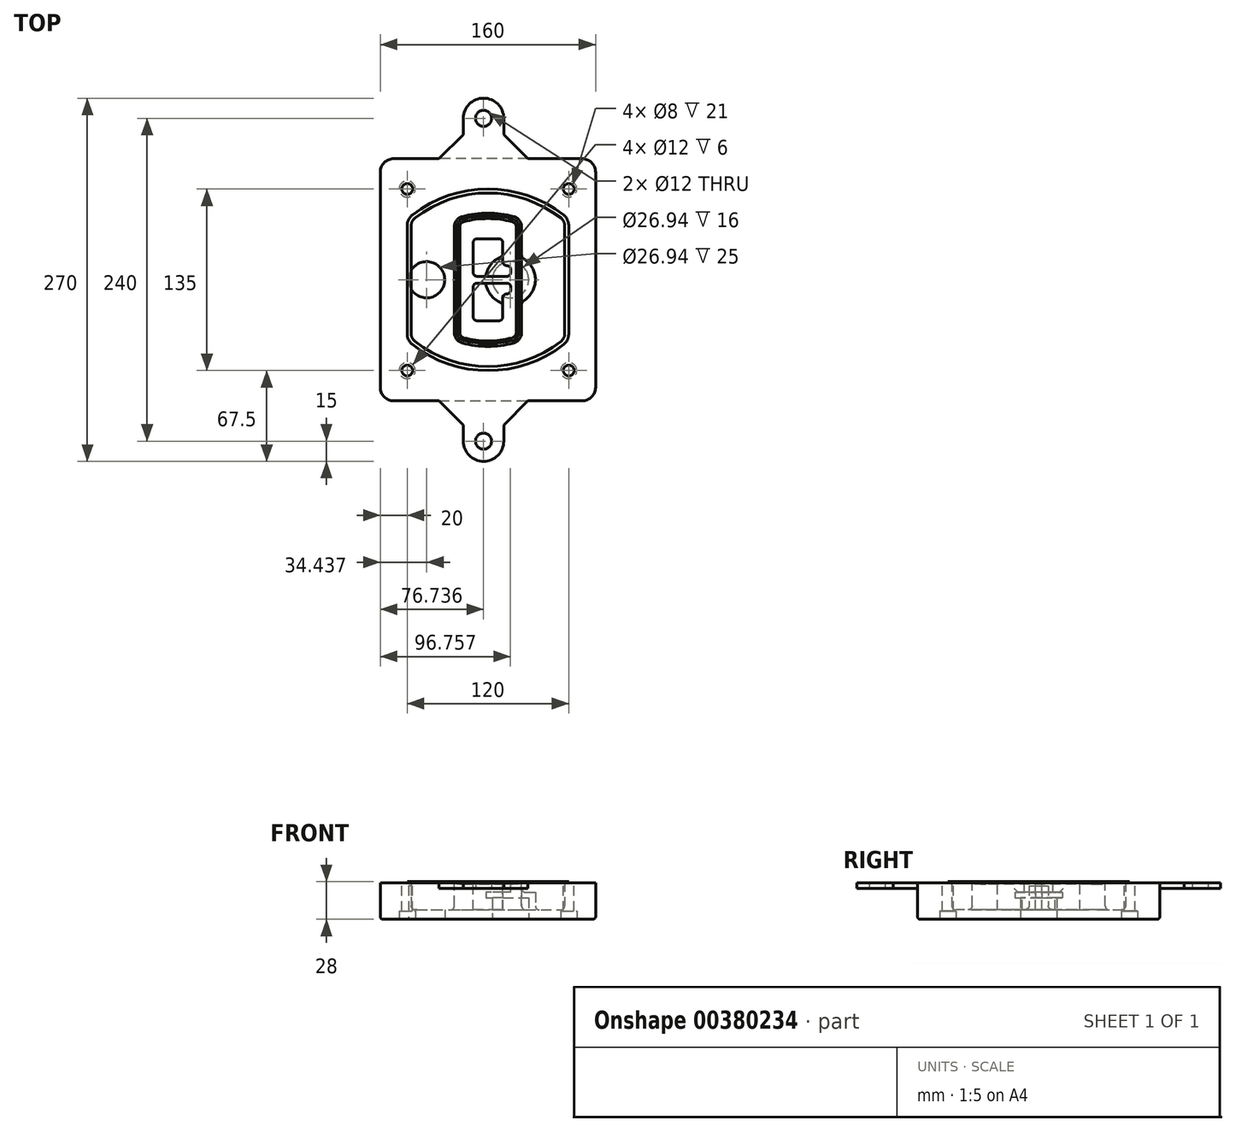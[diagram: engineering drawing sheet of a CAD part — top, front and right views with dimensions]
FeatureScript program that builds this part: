
annotation { "Feature Type Name" : "Feature", "Feature Type Description" : "" }
export const myFeature = defineFeature(function(context is Context, id is Id, definition is map)
    precondition{}
    {
        {
            var Q0;
            Q0=qCreatedBy(makeId("Top.planeOp"),FACE);
            var sketch = newSketch(context, id + "F0", { "sketchPlane" : qUnion([Q0])});
            skPoint(sketch, "E0.rect.middle", {"position": v(0, 0) * mm});
            skLineSegment(sketch, "E1.bottom", {"start": v(-70, -90) * mm, "end": v(70, -90) * mm});
            skLineSegment(sketch, "E1.top", {"start": v(-70, 90) * mm, "end": v(70, 90) * mm});
            skLineSegment(sketch, "E1.left", {"start": v(-80, -80) * mm, "end": v(-80, 80) * mm});
            skLineSegment(sketch, "E1.right", {"start": v(80, -80) * mm, "end": v(80, 80) * mm});
            skLineSegment(sketch, "E2", {"start": v(-80, 90) * mm, "end": v(80, -90) * mm, "construction": true});
            skLineSegment(sketch, "E3", {"start": v(80, 90) * mm, "end": v(-80, -90) * mm, "construction": true});
            skCircle(sketch, "E4", {"center": v(-60, 67.5) * mm, "radius": 4 * mm});
            skCircle(sketch, "E5", {"center": v(60, 67.5) * mm, "radius": 4 * mm});
            skCircle(sketch, "E6", {"center": v(60, -67.5) * mm, "radius": 4 * mm});
            skCircle(sketch, "E7", {"center": v(-60, -67.5) * mm, "radius": 4 * mm});
            skLineSegment(sketch, "E8", {"start": v(-60, 67.5) * mm, "end": v(60, 67.5) * mm, "construction": true});
            skLineSegment(sketch, "E9", {"start": v(60, 67.5) * mm, "end": v(60, -67.5) * mm, "construction": true});
            skLineSegment(sketch, "E10", {"start": v(60, -67.5) * mm, "end": v(-60, -67.5) * mm, "construction": true});
            skLineSegment(sketch, "E11", {"start": v(-60, -67.5) * mm, "end": v(-60, 67.5) * mm, "construction": true});
            skLineSegment(sketch, "E12", {"start": v(-60, 40.3) * mm, "end": v(-60, -40.3) * mm});
            skLineSegment(sketch, "E13", {"start": v(60, 40.3) * mm, "end": v(60, -40.3) * mm});
            skArc(sketch, "E14", {"start": v(56.15, 48.18) * mm, "mid": v(0, 67.5) * mm, "end": v(-56.15, 48.18) * mm});
            skArc(sketch, "E15", {"start": v(-56.15, -48.18) * mm, "mid": v(0, -67.5) * mm, "end": v(56.15, -48.18) * mm});
            skLineSegment(sketch, "E16", {"start": v(-60, 0) * mm, "end": v(60, 0) * mm, "construction": true});
            skPoint(sketch, "E17.visualSharp", {"position": v(-60, -45) * mm});
            skArc(sketch, "E17.filletArc", {"start": v(-60, -40.3) * mm, "mid": v(-58.99, -44.68) * mm, "end": v(-56.15, -48.18) * mm});
            skPoint(sketch, "E18.visualSharp", {"position": v(-60, 45) * mm});
            skArc(sketch, "E18.filletArc", {"start": v(-56.15, 48.18) * mm, "mid": v(-58.99, 44.68) * mm, "end": v(-60, 40.3) * mm});
            skPoint(sketch, "E19.visualSharp", {"position": v(60, 45) * mm});
            skArc(sketch, "E19.filletArc", {"start": v(60, 40.3) * mm, "mid": v(58.99, 44.68) * mm, "end": v(56.15, 48.18) * mm});
            skPoint(sketch, "E20.visualSharp", {"position": v(60, -45) * mm});
            skArc(sketch, "E20.filletArc", {"start": v(56.15, -48.18) * mm, "mid": v(58.99, -44.68) * mm, "end": v(60, -40.3) * mm});
            skPoint(sketch, "E21.visualSharp", {"position": v(-80, 90) * mm});
            skArc(sketch, "E21.filletArc", {"start": v(-70, 90) * mm, "mid": v(-77.07, 87.07) * mm, "end": v(-80, 80) * mm});
            skPoint(sketch, "E22.visualSharp", {"position": v(80, 90) * mm});
            skArc(sketch, "E22.filletArc", {"start": v(80, 80) * mm, "mid": v(77.07, 87.07) * mm, "end": v(70, 90) * mm});
            skPoint(sketch, "E23.visualSharp", {"position": v(80, -90) * mm});
            skArc(sketch, "E23.filletArc", {"start": v(70, -90) * mm, "mid": v(77.07, -87.07) * mm, "end": v(80, -80) * mm});
            skPoint(sketch, "E24.visualSharp", {"position": v(-80, -90) * mm});
            skArc(sketch, "E24.filletArc", {"start": v(-80, -80) * mm, "mid": v(-77.07, -87.07) * mm, "end": v(-70, -90) * mm});
            skArc(sketch, "E25.0", {"start": v(57, 40.3) * mm, "mid": v(56.3, 43.36) * mm, "end": v(54.3, 45.81) * mm});
            skLineSegment(sketch, "E25.1", {"start": v(57, 40.3) * mm, "end": v(57, -40.3) * mm});
            skArc(sketch, "E25.2", {"start": v(54.3, -45.81) * mm, "mid": v(56.3, -43.36) * mm, "end": v(57, -40.3) * mm});
            skArc(sketch, "E25.3", {"start": v(-54.3, -45.81) * mm, "mid": v(0, -64.5) * mm, "end": v(54.3, -45.81) * mm});
            skArc(sketch, "E25.4", {"start": v(-57, -40.3) * mm, "mid": v(-56.3, -43.36) * mm, "end": v(-54.3, -45.81) * mm});
            skArc(sketch, "E25.5", {"start": v(54.3, 45.81) * mm, "mid": v(0, 64.5) * mm, "end": v(-54.3, 45.81) * mm});
            skLineSegment(sketch, "E25.6", {"start": v(-57, 40.3) * mm, "end": v(-57, -40.3) * mm});
            skArc(sketch, "E25.7", {"start": v(-54.3, 45.81) * mm, "mid": v(-56.3, 43.36) * mm, "end": v(-57, 40.3) * mm});
            skArc(sketch, "E26.0", {"start": v(-58.62, 51.33) * mm, "mid": v(-62.58, 46.43) * mm, "end": v(-64, 40.3) * mm});
            skArc(sketch, "E26.1", {"start": v(58.62, 51.33) * mm, "mid": v(0, 71.5) * mm, "end": v(-58.62, 51.33) * mm});
            skArc(sketch, "E26.2", {"start": v(64, 40.3) * mm, "mid": v(62.58, 46.43) * mm, "end": v(58.62, 51.33) * mm});
            skLineSegment(sketch, "E26.3", {"start": v(64, 40.3) * mm, "end": v(64, -40.3) * mm});
            skArc(sketch, "E26.4", {"start": v(58.62, -51.33) * mm, "mid": v(62.58, -46.43) * mm, "end": v(64, -40.3) * mm});
            skLineSegment(sketch, "E26.5", {"start": v(-64, 40.3) * mm, "end": v(-64, -40.3) * mm});
            skArc(sketch, "E26.6", {"start": v(-58.62, -51.33) * mm, "mid": v(0, -71.5) * mm, "end": v(58.62, -51.33) * mm});
            skArc(sketch, "E26.7", {"start": v(-64, -40.3) * mm, "mid": v(-62.58, -46.43) * mm, "end": v(-58.62, -51.33) * mm});
            skSolve(sketch);
        }
        {
            var Q0;
            Q0=makeQuery(id+"F0.imprint","IMPRINT",FACE,{"disambiguationData":[TD([[makeQuery(id+"F0.imprint","IMPRINT",EDGE,{"derivedFrom":sQuery(id+"F0.wireOp",EDGE,"E1.bottom")}),1.0]])]});
            var Q1;
            Q1=makeQuery(id+"F0.imprint","IMPRINT",FACE,{"disambiguationData":[TD([[makeQuery(id+"F0.imprint","IMPRINT",EDGE,{"derivedFrom":sQuery(id+"F0.wireOp",EDGE,"E12")}),1.0]])]});
            var Q2;
            Q2=makeQuery(id+"F0.imprint","IMPRINT",FACE,{"disambiguationData":[TD([[makeQuery(id+"F0.imprint","IMPRINT",EDGE,{"derivedFrom":sQuery(id+"F0.wireOp",EDGE,"E25.0")}),1.0]])]});
            var Q3;
            Q3=makeQuery(id+"F0.imprint","IMPRINT",FACE,{"disambiguationData":[TD([[makeQuery(id+"F0.imprint","IMPRINT",EDGE,{"derivedFrom":sQuery(id+"F0.wireOp",EDGE,"E12")}),-1.0]])]});
            extrude(context, id + "F1", {"entities" : qUnion([Q0, Q1, Q2, Q3]), "oppositeDirection" : true, "depth" : 25 * mm});
        }
        {
            var Q0;
            Q0=makeQuery(id+"F0.imprint","IMPRINT",FACE,{"disambiguationData":[TD([[makeQuery(id+"F0.imprint","IMPRINT",EDGE,{"derivedFrom":sQuery(id+"F0.wireOp",EDGE,"E12")}),1.0]])]});
            extrude(context, id + "F2", {"entities" : qUnion([Q0]), "operationType" : NewBodyOperationType.ADD, "depth" : 3 * mm});
        }
        {
            var Q0;
            Q0=makeQuery(id+"F0.imprint","IMPRINT",FACE,{"disambiguationData":[TD([[makeQuery(id+"F0.imprint","IMPRINT",EDGE,{"derivedFrom":sQuery(id+"F0.wireOp",EDGE,"E25.0")}),1.0]])]});
            extrude(context, id + "F3", {"entities" : qUnion([Q0]), "operationType" : NewBodyOperationType.REMOVE, "oppositeDirection" : true, "depth" : 18 * mm});
        }
        {
            var Q0;
            Q0=makeQuery(id+"F2.opExtrude","CAP_FACE",FACE,{"disambiguationData":[OSD([sQuery(id+"F0.wireOp",EDGE,"E12"),sQuery(id+"F0.wireOp",EDGE,"E13"),sQuery(id+"F0.wireOp",EDGE,"E14"),sQuery(id+"F0.wireOp",EDGE,"E15"),sQuery(id+"F0.wireOp",EDGE,"E17.filletArc"),sQuery(id+"F0.wireOp",EDGE,"E18.filletArc"),sQuery(id+"F0.wireOp",EDGE,"E19.filletArc"),sQuery(id+"F0.wireOp",EDGE,"E20.filletArc"),sQuery(id+"F0.wireOp",EDGE,"E25.0"),sQuery(id+"F0.wireOp",EDGE,"E25.1"),sQuery(id+"F0.wireOp",EDGE,"E25.2"),sQuery(id+"F0.wireOp",EDGE,"E25.3"),sQuery(id+"F0.wireOp",EDGE,"E25.4"),sQuery(id+"F0.wireOp",EDGE,"E25.5"),sQuery(id+"F0.wireOp",EDGE,"E25.6"),sQuery(id+"F0.wireOp",EDGE,"E25.7")])],"isStart":false});
            var sketch = newSketch(context, id + "F4", { "sketchPlane" : qUnion([Q0])});
            skArc(sketch, "E27.0", {"start": v(-19.08, -46.97) * mm, "mid": v(0, -49.5) * mm, "end": v(19.08, -46.97) * mm});
            skArc(sketch, "E28.0", {"start": v(19.08, 46.97) * mm, "mid": v(0, 49.5) * mm, "end": v(-19.08, 46.97) * mm});
            skLineSegment(sketch, "E29", {"start": v(-25, 39.25) * mm, "end": v(-25, -39.25) * mm});
            skLineSegment(sketch, "E30", {"start": v(25, 39.25) * mm, "end": v(25, -39.25) * mm});
            skLineSegment(sketch, "E31", {"start": v(-25, 45.1) * mm, "end": v(25, 45.1) * mm, "construction": true});
            skLineSegment(sketch, "E32", {"start": v(-25, -45.1) * mm, "end": v(25, -45.1) * mm, "construction": true});
            skPoint(sketch, "E33.visualSharp", {"position": v(-25, 45.1) * mm});
            skArc(sketch, "E33.filletArc", {"start": v(-19.08, 46.97) * mm, "mid": v(-23.35, 44.11) * mm, "end": v(-25, 39.25) * mm});
            skPoint(sketch, "E34.visualSharp", {"position": v(25, 45.1) * mm});
            skArc(sketch, "E34.filletArc", {"start": v(25, 39.25) * mm, "mid": v(23.35, 44.11) * mm, "end": v(19.08, 46.97) * mm});
            skPoint(sketch, "E35.visualSharp", {"position": v(25, -45.1) * mm});
            skArc(sketch, "E35.filletArc", {"start": v(19.08, -46.97) * mm, "mid": v(23.35, -44.11) * mm, "end": v(25, -39.25) * mm});
            skPoint(sketch, "E36.visualSharp", {"position": v(-25, -45.1) * mm});
            skArc(sketch, "E36.filletArc", {"start": v(-25, -39.25) * mm, "mid": v(-23.35, -44.11) * mm, "end": v(-19.08, -46.97) * mm});
            skArc(sketch, "E37.0", {"start": v(54.3, 45.81) * mm, "mid": v(0, 64.5) * mm, "end": v(-54.3, 45.81) * mm});
            skArc(sketch, "E37.1", {"start": v(-54.3, 45.81) * mm, "mid": v(-56.3, 43.36) * mm, "end": v(-57, 40.3) * mm});
            skLineSegment(sketch, "E37.2", {"start": v(-57, 40.3) * mm, "end": v(-57, -40.3) * mm});
            skArc(sketch, "E37.3", {"start": v(-57, -40.3) * mm, "mid": v(-56.3, -43.36) * mm, "end": v(-54.3, -45.81) * mm});
            skArc(sketch, "E37.4", {"start": v(-54.3, -45.81) * mm, "mid": v(0, -64.5) * mm, "end": v(54.3, -45.81) * mm});
            skArc(sketch, "E37.5", {"start": v(54.3, -45.81) * mm, "mid": v(56.3, -43.36) * mm, "end": v(57, -40.3) * mm});
            skLineSegment(sketch, "E37.6", {"start": v(57, 40.3) * mm, "end": v(57, -40.3) * mm});
            skArc(sketch, "E37.7", {"start": v(57, 40.3) * mm, "mid": v(56.3, 43.36) * mm, "end": v(54.3, 45.81) * mm});
            skLineSegment(sketch, "E38.0", {"start": v(23, 39.25) * mm, "end": v(23, -39.25) * mm});
            skArc(sketch, "E38.1", {"start": v(18.56, -45.04) * mm, "mid": v(21.76, -42.9) * mm, "end": v(23, -39.25) * mm});
            skArc(sketch, "E38.2", {"start": v(-18.56, -45.04) * mm, "mid": v(0, -47.5) * mm, "end": v(18.56, -45.04) * mm});
            skArc(sketch, "E38.3", {"start": v(-23, -39.25) * mm, "mid": v(-21.76, -42.9) * mm, "end": v(-18.56, -45.04) * mm});
            skLineSegment(sketch, "E38.4", {"start": v(-23, 39.25) * mm, "end": v(-23, -39.25) * mm});
            skArc(sketch, "E38.5", {"start": v(23, 39.25) * mm, "mid": v(21.76, 42.9) * mm, "end": v(18.56, 45.04) * mm});
            skArc(sketch, "E38.6", {"start": v(-18.56, 45.04) * mm, "mid": v(-21.76, 42.9) * mm, "end": v(-23, 39.25) * mm});
            skArc(sketch, "E38.7", {"start": v(18.56, 45.04) * mm, "mid": v(0, 47.5) * mm, "end": v(-18.56, 45.04) * mm});
            skArc(sketch, "E39.0", {"start": v(21, 39.25) * mm, "mid": v(20.18, 41.68) * mm, "end": v(18.04, 43.1) * mm});
            skLineSegment(sketch, "E39.1", {"start": v(21, 39.25) * mm, "end": v(21, -39.25) * mm});
            skArc(sketch, "E39.2", {"start": v(18.04, -43.1) * mm, "mid": v(20.18, -41.68) * mm, "end": v(21, -39.25) * mm});
            skArc(sketch, "E39.3", {"start": v(-18.04, -43.1) * mm, "mid": v(0, -45.5) * mm, "end": v(18.04, -43.1) * mm});
            skArc(sketch, "E39.4", {"start": v(-21, -39.25) * mm, "mid": v(-20.18, -41.68) * mm, "end": v(-18.04, -43.1) * mm});
            skArc(sketch, "E39.5", {"start": v(18.04, 43.1) * mm, "mid": v(0, 45.5) * mm, "end": v(-18.04, 43.1) * mm});
            skLineSegment(sketch, "E39.6", {"start": v(-21, 39.25) * mm, "end": v(-21, -39.25) * mm});
            skArc(sketch, "E39.7", {"start": v(-18.04, 43.1) * mm, "mid": v(-20.18, 41.68) * mm, "end": v(-21, 39.25) * mm});
            skLineSegment(sketch, "E40", {"start": v(-25, 0) * mm, "end": v(25, 0) * mm, "construction": true});
            skLineSegment(sketch, "E41", {"start": v(-11, 5.5) * mm, "end": v(-11, 27.5) * mm});
            skLineSegment(sketch, "E42", {"start": v(-8, 30.5) * mm, "end": v(8, 30.5) * mm});
            skLineSegment(sketch, "E43", {"start": v(11, 27.5) * mm, "end": v(11, 13.5) * mm});
            skLineSegment(sketch, "E44", {"start": v(14, 10.5) * mm, "end": v(14, 10.5) * mm});
            skLineSegment(sketch, "E45", {"start": v(17, 7.5) * mm, "end": v(17, 5.5) * mm});
            skLineSegment(sketch, "E46", {"start": v(14, 2.5) * mm, "end": v(-8, 2.5) * mm});
            skPoint(sketch, "E47.visualSharp", {"position": v(-11, 30.5) * mm});
            skArc(sketch, "E47.filletArc", {"start": v(-8, 30.5) * mm, "mid": v(-10.12, 29.62) * mm, "end": v(-11, 27.5) * mm});
            skPoint(sketch, "E48.visualSharp", {"position": v(11, 30.5) * mm});
            skArc(sketch, "E48.filletArc", {"start": v(11, 27.5) * mm, "mid": v(10.12, 29.62) * mm, "end": v(8, 30.5) * mm});
            skPoint(sketch, "E49.visualSharp", {"position": v(11, 10.5) * mm});
            skArc(sketch, "E49.filletArc", {"start": v(11, 13.5) * mm, "mid": v(11.88, 11.38) * mm, "end": v(14, 10.5) * mm});
            skPoint(sketch, "E50.visualSharp", {"position": v(17, 10.5) * mm});
            skArc(sketch, "E50.filletArc", {"start": v(17, 7.5) * mm, "mid": v(16.12, 9.62) * mm, "end": v(14, 10.5) * mm});
            skPoint(sketch, "E51.visualSharp", {"position": v(17, 2.5) * mm});
            skArc(sketch, "E51.filletArc", {"start": v(14, 2.5) * mm, "mid": v(16.12, 3.38) * mm, "end": v(17, 5.5) * mm});
            skPoint(sketch, "E52.visualSharp", {"position": v(-11, 2.5) * mm});
            skArc(sketch, "E52.filletArc", {"start": v(-11, 5.5) * mm, "mid": v(-10.12, 3.38) * mm, "end": v(-8, 2.5) * mm});
            skLineSegment(sketch, "E53.0.MirrorCS", {"start": v(14, -2.5) * mm, "end": v(-8, -2.5) * mm});
            skArc(sketch, "E54.0.MirrorCS", {"start": v(-11, -5.5) * mm, "mid": v(-10.12, -3.38) * mm, "end": v(-8, -2.5) * mm});
            skLineSegment(sketch, "E55.0.MirrorCS", {"start": v(-11, -5.5) * mm, "end": v(-11, -27.5) * mm});
            skArc(sketch, "E56.0.MirrorCS", {"start": v(-8, -30.5) * mm, "mid": v(-10.12, -29.62) * mm, "end": v(-11, -27.5) * mm});
            skLineSegment(sketch, "E57.0.MirrorCS", {"start": v(-8, -30.5) * mm, "end": v(8, -30.5) * mm});
            skArc(sketch, "E58.0.MirrorCS", {"start": v(11, -27.5) * mm, "mid": v(10.12, -29.62) * mm, "end": v(8, -30.5) * mm});
            skLineSegment(sketch, "E59.0.MirrorCS", {"start": v(11, -27.5) * mm, "end": v(11, -13.5) * mm});
            skArc(sketch, "E60.0.MirrorCS", {"start": v(11, -13.5) * mm, "mid": v(11.88, -11.38) * mm, "end": v(14, -10.5) * mm});
            skArc(sketch, "E61.0.MirrorCS", {"start": v(17, -7.5) * mm, "mid": v(16.12, -9.62) * mm, "end": v(14, -10.5) * mm});
            skLineSegment(sketch, "E62.0.MirrorCS", {"start": v(17, -7.5) * mm, "end": v(17, -5.5) * mm});
            skArc(sketch, "E63.0.MirrorCS", {"start": v(14, -2.5) * mm, "mid": v(16.12, -3.38) * mm, "end": v(17, -5.5) * mm});
            skSolve(sketch);
        }
        {
            var Q0;
            Q0=makeQuery(id+"F4.imprint","IMPRINT",FACE,{"disambiguationData":[TD([[makeQuery(id+"F4.imprint","IMPRINT",EDGE,{"derivedFrom":sQuery(id+"F4.wireOp",EDGE,"E27.0")}),1.0]])]});
            var Q1;
            Q1=makeQuery(id+"F4.imprint","IMPRINT",FACE,{"disambiguationData":[TD([[makeQuery(id+"F4.imprint","IMPRINT",EDGE,{"derivedFrom":sQuery(id+"F4.wireOp",EDGE,"E38.0")}),-1.0]])]});
            var Q2;
            Q2=makeQuery(id+"F4.imprint","IMPRINT",FACE,{"disambiguationData":[TD([[makeQuery(id+"F4.imprint","IMPRINT",EDGE,{"derivedFrom":sQuery(id+"F4.wireOp",EDGE,"E39.0")}),1.0]])]});
            extrude(context, id + "F5", {"entities" : qUnion([Q0, Q1, Q2]), "operationType" : NewBodyOperationType.ADD, "endBound" : BoundingType.UP_TO_NEXT, "oppositeDirection" : true, "depth" : 25 * mm});
        }
        {
            var Q0;
            Q0=makeQuery(id+"F4.imprint","IMPRINT",FACE,{"disambiguationData":[TD([[makeQuery(id+"F4.imprint","IMPRINT",EDGE,{"derivedFrom":sQuery(id+"F4.wireOp",EDGE,"E38.0")}),-1.0]])]});
            extrude(context, id + "F6", {"entities" : qUnion([Q0]), "operationType" : NewBodyOperationType.REMOVE, "oppositeDirection" : true, "depth" : 2 * mm});
        }
        {
            var Q0;
            Q0=makeQuery(id+"F1.opExtrude","CAP_FACE",FACE,{"disambiguationData":[OSD([sQuery(id+"F0.wireOp",EDGE,"E1.bottom"),sQuery(id+"F0.wireOp",EDGE,"E1.top"),sQuery(id+"F0.wireOp",EDGE,"E1.left"),sQuery(id+"F0.wireOp",EDGE,"E1.right"),sQuery(id+"F0.wireOp",EDGE,"E4"),sQuery(id+"F0.wireOp",EDGE,"E5"),sQuery(id+"F0.wireOp",EDGE,"E6"),sQuery(id+"F0.wireOp",EDGE,"E7"),sQuery(id+"F0.wireOp",EDGE,"E21.filletArc"),sQuery(id+"F0.wireOp",EDGE,"E22.filletArc"),sQuery(id+"F0.wireOp",EDGE,"E23.filletArc"),sQuery(id+"F0.wireOp",EDGE,"E24.filletArc")])],"isStart":false});
            var sketch = newSketch(context, id + "F7", { "sketchPlane" : qUnion([Q0])});
            skCircle(sketch, "E64", {"center": v(16.76, 0) * mm, "radius": 13.47 * mm});
            skCircle(sketch, "E65", {"center": v(-45.56, 0) * mm, "radius": 13.47 * mm});
            skLineSegment(sketch, "E66", {"start": v(80, 0) * mm, "end": v(-80, 0) * mm});
            skCircle(sketch, "E67", {"center": v(16.76, 0) * mm, "radius": 18.47 * mm});
            skCircle(sketch, "E68", {"center": v(60, -67.5) * mm, "radius": 6 * mm});
            skCircle(sketch, "E69", {"center": v(-60, -67.5) * mm, "radius": 6 * mm});
            skCircle(sketch, "E70", {"center": v(-60, 67.5) * mm, "radius": 6 * mm});
            skCircle(sketch, "E71", {"center": v(60, 67.5) * mm, "radius": 6 * mm});
            skSolve(sketch);
        }
        {
            var Q0;
            {var subQ1=sQuery(id+"F7.wireOp",EDGE,"E66");var subQ4=sQuery(id+"F7.wireOp",EDGE,"E64");var subQ6=makeQuery(id+"F7.imprint","INTERSECT",VERTEX,{"disambiguationData":[OD(0.0)],"derivedFrom":[subQ4,subQ1]});Q0=makeQuery(id+"F7.imprint","IMPRINT",FACE,{"disambiguationData":[TD([[makeQuery(id+"F7.imprint","IMPRINT",EDGE,{"disambiguationData":[TD([[subQ6,-1.0]])],"derivedFrom":subQ4}),-1.0]])]});}
            var Q1;
            {var subQ0=sQuery(id+"F7.wireOp",EDGE,"E66");var subQ1=sQuery(id+"F7.wireOp",EDGE,"E64");var subQ3=makeQuery(id+"F7.imprint","INTERSECT",VERTEX,{"disambiguationData":[OD(0.0)],"derivedFrom":[subQ1,subQ0]});Q1=makeQuery(id+"F7.imprint","IMPRINT",FACE,{"disambiguationData":[TD([[makeQuery(id+"F7.imprint","IMPRINT",EDGE,{"disambiguationData":[TD([[subQ3,-1.0]])],"derivedFrom":subQ1}),1.0]])]});}
            var Q2;
            {var subQ0=sQuery(id+"F7.wireOp",EDGE,"E66");var subQ1=sQuery(id+"F7.wireOp",EDGE,"E64");var subQ3=makeQuery(id+"F7.imprint","INTERSECT",VERTEX,{"disambiguationData":[OD(0.0)],"derivedFrom":[subQ1,subQ0]});Q2=makeQuery(id+"F7.imprint","IMPRINT",FACE,{"disambiguationData":[TD([[makeQuery(id+"F7.imprint","IMPRINT",EDGE,{"disambiguationData":[TD([[subQ3,1.0]])],"derivedFrom":subQ1}),1.0]])]});}
            var Q3;
            {var subQ1=sQuery(id+"F7.wireOp",EDGE,"E66");var subQ4=sQuery(id+"F7.wireOp",EDGE,"E64");var subQ6=makeQuery(id+"F7.imprint","INTERSECT",VERTEX,{"disambiguationData":[OD(0.0)],"derivedFrom":[subQ4,subQ1]});Q3=makeQuery(id+"F7.imprint","IMPRINT",FACE,{"disambiguationData":[TD([[makeQuery(id+"F7.imprint","IMPRINT",EDGE,{"disambiguationData":[TD([[subQ6,1.0]])],"derivedFrom":subQ4}),-1.0]])]});}
            extrude(context, id + "F8", {"entities" : qUnion([Q0, Q1, Q2, Q3]), "operationType" : NewBodyOperationType.ADD, "oppositeDirection" : true, "depth" : 20 * mm});
        }
        {
            var Q0;
            {var subQ0=sQuery(id+"F7.wireOp",EDGE,"E66");var subQ1=sQuery(id+"F7.wireOp",EDGE,"E64");var subQ3=makeQuery(id+"F7.imprint","INTERSECT",VERTEX,{"disambiguationData":[OD(0.0)],"derivedFrom":[subQ1,subQ0]});Q0=makeQuery(id+"F7.imprint","IMPRINT",FACE,{"disambiguationData":[TD([[makeQuery(id+"F7.imprint","IMPRINT",EDGE,{"disambiguationData":[TD([[subQ3,-1.0]])],"derivedFrom":subQ1}),1.0]])]});}
            var Q1;
            {var subQ0=sQuery(id+"F7.wireOp",EDGE,"E66");var subQ1=sQuery(id+"F7.wireOp",EDGE,"E64");var subQ3=makeQuery(id+"F7.imprint","INTERSECT",VERTEX,{"disambiguationData":[OD(0.0)],"derivedFrom":[subQ1,subQ0]});Q1=makeQuery(id+"F7.imprint","IMPRINT",FACE,{"disambiguationData":[TD([[makeQuery(id+"F7.imprint","IMPRINT",EDGE,{"disambiguationData":[TD([[subQ3,1.0]])],"derivedFrom":subQ1}),1.0]])]});}
            extrude(context, id + "F9", {"entities" : qUnion([Q0, Q1]), "operationType" : NewBodyOperationType.REMOVE, "oppositeDirection" : true, "depth" : 16 * mm});
        }
        {
            var Q0;
            {var subQ0=sQuery(id+"F7.wireOp",EDGE,"E66");var subQ1=sQuery(id+"F7.wireOp",EDGE,"E65");var subQ3=makeQuery(id+"F7.imprint","INTERSECT",VERTEX,{"disambiguationData":[OD(0.0)],"derivedFrom":[subQ1,subQ0]});Q0=makeQuery(id+"F7.imprint","IMPRINT",FACE,{"disambiguationData":[TD([[makeQuery(id+"F7.imprint","IMPRINT",EDGE,{"disambiguationData":[TD([[subQ3,-1.0]])],"derivedFrom":subQ1}),1.0]])]});}
            var Q1;
            {var subQ0=sQuery(id+"F7.wireOp",EDGE,"E66");var subQ1=sQuery(id+"F7.wireOp",EDGE,"E65");var subQ3=makeQuery(id+"F7.imprint","INTERSECT",VERTEX,{"disambiguationData":[OD(0.0)],"derivedFrom":[subQ1,subQ0]});Q1=makeQuery(id+"F7.imprint","IMPRINT",FACE,{"disambiguationData":[TD([[makeQuery(id+"F7.imprint","IMPRINT",EDGE,{"disambiguationData":[TD([[subQ3,1.0]])],"derivedFrom":subQ1}),1.0]])]});}
            extrude(context, id + "F10", {"entities" : qUnion([Q0, Q1]), "operationType" : NewBodyOperationType.REMOVE, "oppositeDirection" : true, "depth" : 25 * mm});
        }
        {
            var Q0;
            Q0=makeQuery(id+"F7.imprint","IMPRINT",FACE,{"disambiguationData":[TD([[makeQuery(id+"F7.imprint","IMPRINT",EDGE,{"derivedFrom":sQuery(id+"F7.wireOp",EDGE,"E68")}),1.0]])]});
            var Q1;
            Q1=makeQuery(id+"F7.imprint","IMPRINT",FACE,{"disambiguationData":[TD([[makeQuery(id+"F7.imprint","IMPRINT",EDGE,{"derivedFrom":makeQuery(id+"F1.opExtrude","CAP_EDGE",EDGE,{"disambiguationData":[OSD([sQuery(id+"F0.wireOp",EDGE,"E5")])],"isStart":false})}),-1.0]])]});
            var Q2;
            Q2=makeQuery(id+"F7.imprint","IMPRINT",FACE,{"disambiguationData":[TD([[makeQuery(id+"F7.imprint","IMPRINT",EDGE,{"derivedFrom":sQuery(id+"F7.wireOp",EDGE,"E69")}),1.0]])]});
            var Q3;
            Q3=makeQuery(id+"F7.imprint","IMPRINT",FACE,{"disambiguationData":[TD([[makeQuery(id+"F7.imprint","IMPRINT",EDGE,{"derivedFrom":makeQuery(id+"F1.opExtrude","CAP_EDGE",EDGE,{"disambiguationData":[OSD([sQuery(id+"F0.wireOp",EDGE,"E4")])],"isStart":false})}),-1.0]])]});
            var Q4;
            Q4=makeQuery(id+"F7.imprint","IMPRINT",FACE,{"disambiguationData":[TD([[makeQuery(id+"F7.imprint","IMPRINT",EDGE,{"derivedFrom":sQuery(id+"F7.wireOp",EDGE,"E70")}),1.0]])]});
            var Q5;
            Q5=makeQuery(id+"F7.imprint","IMPRINT",FACE,{"disambiguationData":[TD([[makeQuery(id+"F7.imprint","IMPRINT",EDGE,{"derivedFrom":makeQuery(id+"F1.opExtrude","CAP_EDGE",EDGE,{"disambiguationData":[OSD([sQuery(id+"F0.wireOp",EDGE,"E7")])],"isStart":false})}),-1.0]])]});
            var Q6;
            Q6=makeQuery(id+"F7.imprint","IMPRINT",FACE,{"disambiguationData":[TD([[makeQuery(id+"F7.imprint","IMPRINT",EDGE,{"derivedFrom":sQuery(id+"F7.wireOp",EDGE,"E71")}),1.0]])]});
            var Q7;
            Q7=makeQuery(id+"F7.imprint","IMPRINT",FACE,{"disambiguationData":[TD([[makeQuery(id+"F7.imprint","IMPRINT",EDGE,{"derivedFrom":makeQuery(id+"F1.opExtrude","CAP_EDGE",EDGE,{"disambiguationData":[OSD([sQuery(id+"F0.wireOp",EDGE,"E6")])],"isStart":false})}),-1.0]])]});
            extrude(context, id + "F11", {"entities" : qUnion([Q0, Q1, Q2, Q3, Q4, Q5, Q6, Q7]), "operationType" : NewBodyOperationType.REMOVE, "oppositeDirection" : true, "depth" : 6 * mm});
        }
        {
            var Q0;
            Q0=makeQuery(id+"F9.boolean.opBoolean","COPY",FACE,{"derivedFrom":makeQuery(id+"F9.opExtrude","CAP_FACE",FACE,{"disambiguationData":[OSD([sQuery(id+"F7.wireOp",EDGE,"E64")])],"isStart":false})});
            var sketch = newSketch(context, id + "F12", { "sketchPlane" : qUnion([Q0])});
            skArc(sketch, "E72.0", {"start": v(11, 17.55) * mm, "mid": v(2.57, 11.82) * mm, "end": v(-1.54, 2.5) * mm});
            skArc(sketch, "E72.1", {"start": v(-1.54, -2.5) * mm, "mid": v(2.57, -11.82) * mm, "end": v(11, -17.55) * mm});
            skLineSegment(sketch, "E73", {"start": v(-1.54, -2.5) * mm, "end": v(14, -2.5) * mm});
            skLineSegment(sketch, "E74.0", {"start": v(14, 2.5) * mm, "end": v(-1.54, 2.5) * mm});
            skArc(sketch, "E74.1", {"start": v(14, 2.5) * mm, "mid": v(16.12, 3.38) * mm, "end": v(17, 5.5) * mm});
            skLineSegment(sketch, "E74.2", {"start": v(17, 7.5) * mm, "end": v(17, 5.5) * mm});
            skArc(sketch, "E74.3", {"start": v(17, 7.5) * mm, "mid": v(16.12, 9.62) * mm, "end": v(14, 10.5) * mm});
            skArc(sketch, "E74.4", {"start": v(11, 13.5) * mm, "mid": v(11.88, 11.38) * mm, "end": v(14, 10.5) * mm});
            skLineSegment(sketch, "E74.5", {"start": v(11, 17.55) * mm, "end": v(11, 13.5) * mm});
            skLineSegment(sketch, "E74.7", {"start": v(14, -2.5) * mm, "end": v(-1.54, -2.5) * mm});
            skArc(sketch, "E74.8", {"start": v(14, -2.5) * mm, "mid": v(16.12, -3.38) * mm, "end": v(17, -5.5) * mm});
            skLineSegment(sketch, "E74.9", {"start": v(17, -7.5) * mm, "end": v(17, -5.5) * mm});
            skArc(sketch, "E74.10", {"start": v(17, -7.5) * mm, "mid": v(16.12, -9.62) * mm, "end": v(14, -10.5) * mm});
            skArc(sketch, "E74.11", {"start": v(11, -13.5) * mm, "mid": v(11.88, -11.38) * mm, "end": v(14, -10.5) * mm});
            skLineSegment(sketch, "E74.12", {"start": v(11, -17.55) * mm, "end": v(11, -13.5) * mm});
            skPoint(sketch, "E75.orphan", {"position": v(11, -27.5) * mm});
            skPoint(sketch, "E76.orphan", {"position": v(-8, -2.5) * mm});
            skPoint(sketch, "E77.orphan", {"position": v(-8, 2.5) * mm});
            skPoint(sketch, "E78.orphan", {"position": v(11, 27.5) * mm});
            skSolve(sketch);
        }
        {
            var Q0;
            {var subQ7=sQuery(id+"F12.wireOp",EDGE,"E72.0");var subQ14=sQuery(id+"F12.wireOp",EDGE,"E72.1");var subQ16=sQuery(id+"F12.wireOp",EDGE,"E74.1");var subQ18=sQuery(id+"F12.wireOp",EDGE,"E74.8");Q0=qUnion([makeQuery(id+"F12.imprint","IMPRINT",FACE,{"disambiguationData":[TD([[makeQuery(id+"F12.imprint","IMPRINT",EDGE,{"derivedFrom":subQ7}),1.0]])]}),makeQuery(id+"F12.imprint","IMPRINT",FACE,{"disambiguationData":[TD([[makeQuery(id+"F12.imprint","IMPRINT",EDGE,{"derivedFrom":subQ14}),1.0]])]}),makeQuery(id+"F12.imprint","IMPRINT",FACE,{"disambiguationData":[TD([[makeQuery(id+"F12.imprint","IMPRINT",EDGE,{"derivedFrom":subQ16}),1.0]])]}),makeQuery(id+"F12.imprint","IMPRINT",FACE,{"disambiguationData":[TD([[makeQuery(id+"F12.imprint","IMPRINT",EDGE,{"derivedFrom":subQ18}),-1.0]])]})]);}
            var Q1;
            Q1=makeQuery(id+"F5.boolean.opBoolean","SPLIT",FACE,{"disambiguationData":[TD([makeQuery(id+"F5.opExtrude","SWEPT_FACE",FACE,{"disambiguationData":[OSD([sQuery(id+"F4.wireOp",EDGE,"E41")])]})])],"derivedFrom":makeQuery(id+"F3.boolean.opBoolean","COPY",FACE,{"derivedFrom":makeQuery(id+"F3.opExtrude","CAP_FACE",FACE,{"disambiguationData":[OSD([sQuery(id+"F0.wireOp",EDGE,"E25.0"),sQuery(id+"F0.wireOp",EDGE,"E25.1"),sQuery(id+"F0.wireOp",EDGE,"E25.2"),sQuery(id+"F0.wireOp",EDGE,"E25.3"),sQuery(id+"F0.wireOp",EDGE,"E25.4"),sQuery(id+"F0.wireOp",EDGE,"E25.5"),sQuery(id+"F0.wireOp",EDGE,"E25.6"),sQuery(id+"F0.wireOp",EDGE,"E25.7")])],"isStart":false})})});
            extrude(context, id + "F13", {"entities" : qUnion([Q0]), "operationType" : NewBodyOperationType.REMOVE, "endBound" : BoundingType.UP_TO_SURFACE, "endBoundEntityFace" : qUnion([Q1]), "depth" : 25 * mm});
        }
        {
            var Q0;
            Q0=makeQuery(id+"F3.boolean.opBoolean","COPY",EDGE,{"derivedFrom":makeQuery(id+"F3.opExtrude","CAP_EDGE",EDGE,{"disambiguationData":[OSD([sQuery(id+"F0.wireOp",EDGE,"E25.6")])],"isStart":false})});
            var Q1;
            Q1=makeQuery(id+"F8.boolean.opBoolean","INTERSECT",EDGE,{"derivedFrom":[makeQuery(id+"F5.opExtrude","SWEPT_FACE",FACE,{"disambiguationData":[OSD([sQuery(id+"F4.wireOp",EDGE,"E30")])]}),makeQuery(id+"F8.opExtrude","CAP_FACE",FACE,{"disambiguationData":[OSD([sQuery(id+"F7.wireOp",EDGE,"E67")])],"isStart":false})]});
            var Q2;
            Q2=makeQuery(id+"F8.boolean.opBoolean","INTERSECT",EDGE,{"disambiguationData":[OD(1.0)],"derivedFrom":[makeQuery(id+"F5.opExtrude","SWEPT_FACE",FACE,{"disambiguationData":[OSD([sQuery(id+"F4.wireOp",EDGE,"E30")])]}),makeQuery(id+"F8.opExtrude","SWEPT_FACE",FACE,{"disambiguationData":[OSD([sQuery(id+"F7.wireOp",EDGE,"E67")])]})]});
            var Q3;
            {var subQ0=sQuery(id+"F4.wireOp",EDGE,"E30");Q3=makeQuery(id+"F8.boolean.opBoolean","SPLIT",EDGE,{"disambiguationData":[TD([makeQuery(id+"F5.opExtrude","SWEPT_FACE",FACE,{"disambiguationData":[OSD([sQuery(id+"F4.wireOp",EDGE,"E35.filletArc")])]})])],"derivedFrom":makeQuery(id+"F5.opExtrude","CAP_EDGE",EDGE,{"disambiguationData":[OSD([subQ0])],"isStart":false})});}
            var Q4;
            {var subQ0=sQuery(id+"F0.wireOp",EDGE,"E25.7");var subQ1=sQuery(id+"F0.wireOp",EDGE,"E25.1");var subQ2=sQuery(id+"F0.wireOp",EDGE,"E25.6");var subQ3=sQuery(id+"F0.wireOp",EDGE,"E25.5");var subQ4=sQuery(id+"F0.wireOp",EDGE,"E25.4");var subQ5=sQuery(id+"F0.wireOp",EDGE,"E25.0");var subQ6=sQuery(id+"F0.wireOp",EDGE,"E25.2");var subQ7=sQuery(id+"F0.wireOp",EDGE,"E25.3");Q4=makeQuery(id+"F8.boolean.opBoolean","INTERSECT",EDGE,{"derivedFrom":[makeQuery(id+"F5.boolean.opBoolean","SPLIT",FACE,{"disambiguationData":[TD([makeQuery(id+"F2.opExtrude","SWEPT_FACE",FACE,{"disambiguationData":[OSD([subQ5])]})])],"derivedFrom":makeQuery(id+"F3.boolean.opBoolean","COPY",FACE,{"derivedFrom":makeQuery(id+"F3.opExtrude","CAP_FACE",FACE,{"disambiguationData":[OSD([subQ5,subQ1,subQ6,subQ7,subQ4,subQ3,subQ2,subQ0])],"isStart":false})})}),makeQuery(id+"F8.opExtrude","SWEPT_FACE",FACE,{"disambiguationData":[OSD([sQuery(id+"F7.wireOp",EDGE,"E67")])]})]});}
            var Q5;
            Q5=makeQuery(id+"F8.boolean.opBoolean","INTERSECT",EDGE,{"disambiguationData":[OD(0.0)],"derivedFrom":[makeQuery(id+"F5.opExtrude","SWEPT_FACE",FACE,{"disambiguationData":[OSD([sQuery(id+"F4.wireOp",EDGE,"E30")])]}),makeQuery(id+"F8.opExtrude","SWEPT_FACE",FACE,{"disambiguationData":[OSD([sQuery(id+"F7.wireOp",EDGE,"E67")])]})]});
            fillet(context, id + "F14", {"entities" : qUnion([Q0, Q1, Q2, Q3, Q4, Q5]), "radius" : 3 * mm, "tangentPropagation" : true, "allowEdgeOverflow" : false});
        }
        {
            var Q0;
            Q0=makeQuery(id+"F1.opExtrude","CAP_EDGE",EDGE,{"disambiguationData":[OSD([sQuery(id+"F0.wireOp",EDGE,"E1.bottom")])],"isStart":false});
            fillet(context, id + "F15", {"entities" : qUnion([Q0]), "radius" : 2 * mm, "tangentPropagation" : true, "allowEdgeOverflow" : false});
        }
        {
            var Q0;
            {var subQ0=sQuery(id+"F0.wireOp",EDGE,"E21.filletArc");var subQ1=sQuery(id+"F0.wireOp",EDGE,"E7");var subQ2=sQuery(id+"F0.wireOp",EDGE,"E6");var subQ3=sQuery(id+"F0.wireOp",EDGE,"E5");var subQ4=sQuery(id+"F0.wireOp",EDGE,"E4");var subQ5=sQuery(id+"F0.wireOp",EDGE,"E22.filletArc");var subQ6=sQuery(id+"F0.wireOp",EDGE,"E1.bottom");var subQ7=sQuery(id+"F0.wireOp",EDGE,"E1.right");var subQ8=sQuery(id+"F0.wireOp",EDGE,"E1.top");var subQ9=sQuery(id+"F0.wireOp",EDGE,"E1.left");var subQ10=sQuery(id+"F0.wireOp",EDGE,"E23.filletArc");var subQ11=sQuery(id+"F0.wireOp",EDGE,"E24.filletArc");Q0=makeQuery(id+"F2.boolean.opBoolean","SPLIT",FACE,{"disambiguationData":[TD([makeQuery(id+"F1.opExtrude","SWEPT_FACE",FACE,{"disambiguationData":[OSD([subQ6])]})])],"derivedFrom":makeQuery(id+"F1.opExtrude","CAP_FACE",FACE,{"disambiguationData":[OSD([subQ6,subQ8,subQ9,subQ7,subQ4,subQ3,subQ2,subQ1,subQ0,subQ5,subQ10,subQ11])],"isStart":true})});}
            var sketch = newSketch(context, id + "F16", { "sketchPlane" : qUnion([Q0])});
            skLineSegment(sketch, "E79", {"start": v(-36.26, 90) * mm, "end": v(-18.26, 108) * mm});
            skLineSegment(sketch, "E80", {"start": v(-18.26, 108) * mm, "end": v(-18.26, 120) * mm});
            skLineSegment(sketch, "E81", {"start": v(11.74, 120) * mm, "end": v(11.74, 108) * mm});
            skLineSegment(sketch, "E82", {"start": v(11.74, 108) * mm, "end": v(29.74, 90) * mm});
            skArc(sketch, "E83", {"start": v(-18.26, 120) * mm, "mid": v(-3.26, 135) * mm, "end": v(11.74, 120) * mm});
            skCircle(sketch, "E84", {"center": v(-3.26, 120) * mm, "radius": 6 * mm});
            skLineSegment(sketch, "E85", {"start": v(-80, 0) * mm, "end": v(80, 0) * mm, "construction": true});
            skLineSegment(sketch, "E86.MirrorCS", {"start": v(11.74, -108) * mm, "end": v(29.74, -90) * mm});
            skLineSegment(sketch, "E87.MirrorCS", {"start": v(11.74, -120) * mm, "end": v(11.74, -108) * mm});
            skArc(sketch, "E88.MirrorCS", {"start": v(-18.26, -120) * mm, "mid": v(-3.26, -135) * mm, "end": v(11.74, -120) * mm});
            skLineSegment(sketch, "E89.MirrorCS", {"start": v(-18.26, -108) * mm, "end": v(-18.26, -120) * mm});
            skLineSegment(sketch, "E90.MirrorCS", {"start": v(-36.26, -90) * mm, "end": v(-18.26, -108) * mm});
            skCircle(sketch, "E91.MirrorC", {"center": v(-3.26, -120) * mm, "radius": 6 * mm});
            skSolve(sketch);
        }
        {
            var Q0;
            {var subQ1=sQuery(id+"F16.wireOp",EDGE,"E79");Q0=makeQuery(id+"F16.imprint","IMPRINT",FACE,{"disambiguationData":[TD([[makeQuery(id+"F16.imprint","IMPRINT",EDGE,{"derivedFrom":subQ1}),-1.0]])]});}
            var Q1;
            {var subQ0=sQuery(id+"F16.wireOp",EDGE,"E86.MirrorCS");Q1=makeQuery(id+"F16.imprint","IMPRINT",FACE,{"disambiguationData":[TD([[makeQuery(id+"F16.imprint","IMPRINT",EDGE,{"derivedFrom":subQ0}),1.0]])]});}
            var Q2;
            Q2=makeQuery(id+"F16.imprint","IMPRINT",FACE,{"disambiguationData":[TD([[makeQuery(id+"F16.imprint","IMPRINT",EDGE,{"derivedFrom":makeQuery(id+"F1.opExtrude","CAP_EDGE",EDGE,{"disambiguationData":[OSD([sQuery(id+"F0.wireOp",EDGE,"E1.left")])],"isStart":true})}),-1.0]])]});
            extrude(context, id + "F17", {"entities" : qUnion([Q0, Q1, Q2]), "operationType" : NewBodyOperationType.ADD, "endBound" : BoundingType.SYMMETRIC, "depth" : 4 * mm});
        }
    });
